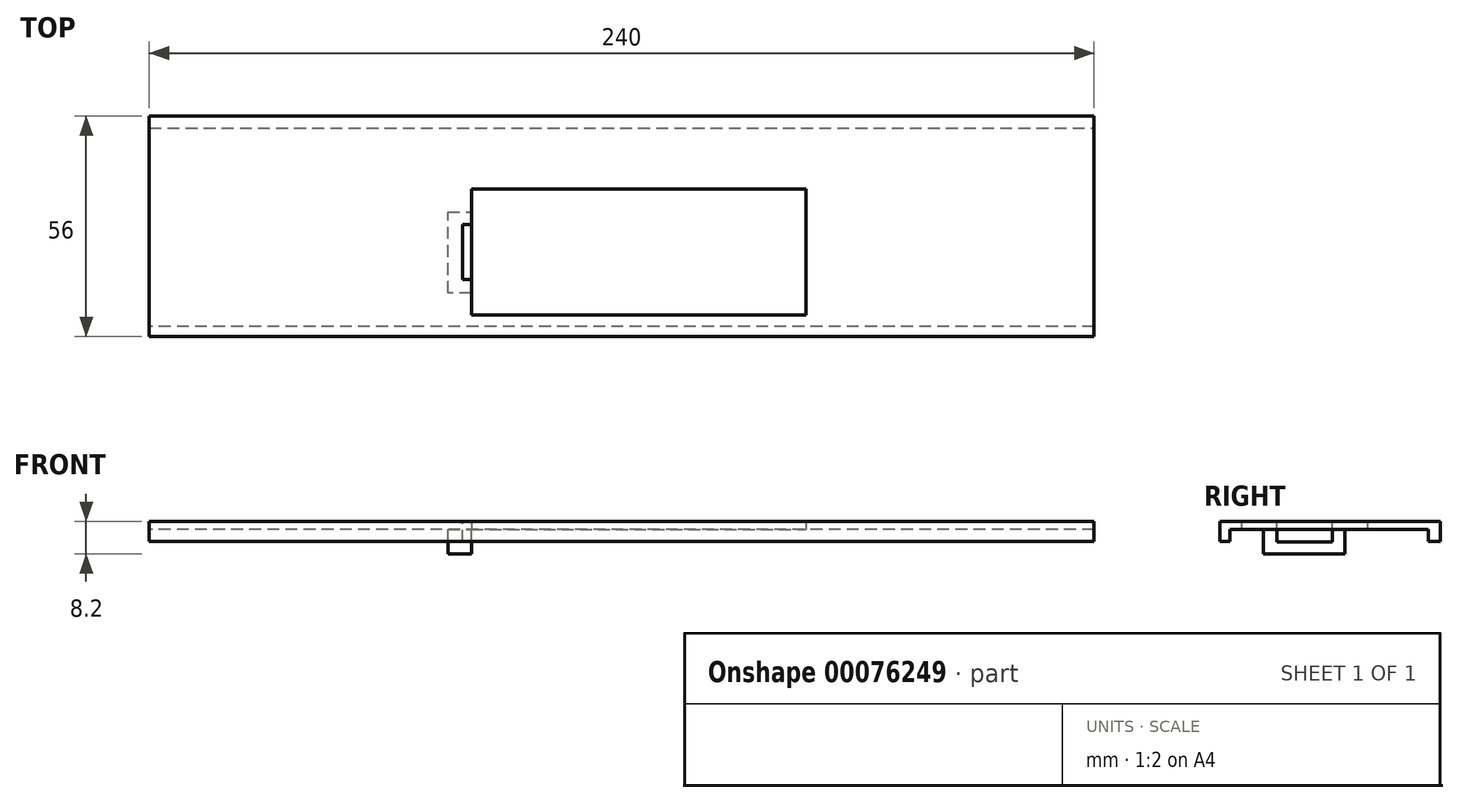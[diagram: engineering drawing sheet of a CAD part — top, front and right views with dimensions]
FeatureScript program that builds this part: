
annotation { "Feature Type Name" : "Feature", "Feature Type Description" : "" }
export const myFeature = defineFeature(function(context is Context, id is Id, definition is map)
    precondition{}
    {
        {
            var Q0;
            Q0=qCreatedBy(makeId("Top.planeOp"),FACE);
            var sketch = newSketch(context, id + "F0", { "sketchPlane" : qUnion([Q0])});
            skLineSegment(sketch, "E0.bottom", {"start": v(-106.36, 0) * mm, "end": v(133.64, 0) * mm});
            skLineSegment(sketch, "E0.top", {"start": v(-106.36, 56) * mm, "end": v(133.64, 56) * mm});
            skLineSegment(sketch, "E0.left", {"start": v(-106.36, 0) * mm, "end": v(-106.36, 56) * mm});
            skLineSegment(sketch, "E0.right", {"start": v(133.64, 0) * mm, "end": v(133.64, 56) * mm});
            skLineSegment(sketch, "E1.bottom", {"start": v(-24.53, 37.5) * mm, "end": v(60.47, 37.5) * mm});
            skLineSegment(sketch, "E1.top", {"start": v(-24.53, 5.5) * mm, "end": v(60.47, 5.5) * mm});
            skLineSegment(sketch, "E1.left", {"start": v(-24.53, 37.5) * mm, "end": v(-24.53, 5.5) * mm});
            skLineSegment(sketch, "E1.right", {"start": v(60.47, 37.5) * mm, "end": v(60.47, 5.5) * mm});
            skSolve(sketch);
        }
        {
            var Q0;
            Q0=makeQuery(id+"F0.imprint","IMPRINT",FACE,{"disambiguationData":[TD([[makeQuery(id+"F0.imprint","IMPRINT",EDGE,{"derivedFrom":sQuery(id+"F0.wireOp",EDGE,"E0.bottom")}),1.0]])]});
            extrude(context, id + "F1", {"entities" : qUnion([Q0]), "depth" : 2 * mm});
        }
        {
            var Q0;
            Q0=makeQuery(id+"F1.opExtrude","CAP_FACE",FACE,{"disambiguationData":[OSD([sQuery(id+"F0.wireOp",EDGE,"E0.bottom"),sQuery(id+"F0.wireOp",EDGE,"E0.top"),sQuery(id+"F0.wireOp",EDGE,"E0.left"),sQuery(id+"F0.wireOp",EDGE,"E0.right"),sQuery(id+"F0.wireOp",EDGE,"E1.bottom"),sQuery(id+"F0.wireOp",EDGE,"E1.top"),sQuery(id+"F0.wireOp",EDGE,"E1.left"),sQuery(id+"F0.wireOp",EDGE,"E1.right")])],"isStart":false});
            var sketch = newSketch(context, id + "F2", { "sketchPlane" : qUnion([Q0])});
            skLineSegment(sketch, "E2", {"start": v(-24.53, 37.5) * mm, "end": v(-24.53, 28.5) * mm});
            skLineSegment(sketch, "E3", {"start": v(-24.53, 5.5) * mm, "end": v(-24.53, 14.5) * mm});
            skLineSegment(sketch, "E4", {"start": v(-24.53, 14.5) * mm, "end": v(-26.73, 14.5) * mm});
            skLineSegment(sketch, "E5", {"start": v(-24.53, 28.5) * mm, "end": v(-26.73, 28.5) * mm});
            skLineSegment(sketch, "E6", {"start": v(-26.73, 14.5) * mm, "end": v(-26.73, 28.5) * mm});
            skSolve(sketch);
        }
        {
            var Q0;
            {var subQ0=sQuery(id+"F2.wireOp",EDGE,"E4");Q0=makeQuery(id+"F2.imprint","IMPRINT",FACE,{"disambiguationData":[TD([[makeQuery(id+"F2.imprint","IMPRINT",EDGE,{"derivedFrom":subQ0}),-1.0]])]});}
            extrude(context, id + "F3", {"entities" : qUnion([Q0]), "operationType" : NewBodyOperationType.REMOVE, "oppositeDirection" : true, "depth" : 25 * mm});
        }
        {
            var Q0;
            Q0=makeQuery(id+"F1.opExtrude","CAP_FACE",FACE,{"disambiguationData":[OSD([sQuery(id+"F0.wireOp",EDGE,"E0.bottom"),sQuery(id+"F0.wireOp",EDGE,"E0.top"),sQuery(id+"F0.wireOp",EDGE,"E0.left"),sQuery(id+"F0.wireOp",EDGE,"E0.right"),sQuery(id+"F0.wireOp",EDGE,"E1.bottom"),sQuery(id+"F0.wireOp",EDGE,"E1.top"),sQuery(id+"F0.wireOp",EDGE,"E1.left"),sQuery(id+"F0.wireOp",EDGE,"E1.right")])],"isStart":true});
            var sketch = newSketch(context, id + "F4", { "sketchPlane" : qUnion([Q0])});
            skLineSegment(sketch, "E7", {"start": v(-24.53, -11.05) * mm, "end": v(-30.5, -11.05) * mm});
            skLineSegment(sketch, "E8", {"start": v(-30.5, -11.05) * mm, "end": v(-30.5, -31.68) * mm});
            skLineSegment(sketch, "E9", {"start": v(-24.53, -31.68) * mm, "end": v(-24.53, -28.5) * mm});
            skLineSegment(sketch, "E10", {"start": v(-24.53, -28.5) * mm, "end": v(-26.73, -28.5) * mm});
            skLineSegment(sketch, "E11", {"start": v(-26.73, -28.5) * mm, "end": v(-26.73, -14.5) * mm});
            skLineSegment(sketch, "E12", {"start": v(-26.73, -14.5) * mm, "end": v(-24.53, -14.5) * mm});
            skLineSegment(sketch, "E13", {"start": v(-24.53, -14.5) * mm, "end": v(-24.53, -11.05) * mm});
            skLineSegment(sketch, "E14", {"start": v(-30.5, -31.68) * mm, "end": v(-24.53, -31.68) * mm});
            skSolve(sketch);
        }
        {
            var Q0;
            Q0=makeQuery(id+"F4.imprint","IMPRINT",FACE,{"disambiguationData":[TD([[makeQuery(id+"F4.imprint","IMPRINT",EDGE,{"derivedFrom":sQuery(id+"F4.wireOp",EDGE,"E7")}),1.0]])]});
            extrude(context, id + "F5", {"entities" : qUnion([Q0]), "operationType" : NewBodyOperationType.ADD, "depth" : 3.2 * mm});
        }
        {
            var Q0;
            Q0=makeQuery(id+"F5.opExtrude","CAP_FACE",FACE,{"disambiguationData":[OSD([sQuery(id+"F4.wireOp",EDGE,"E7"),sQuery(id+"F4.wireOp",EDGE,"E8"),sQuery(id+"F4.wireOp",EDGE,"E9"),sQuery(id+"F4.wireOp",EDGE,"E10"),sQuery(id+"F4.wireOp",EDGE,"E11"),sQuery(id+"F4.wireOp",EDGE,"E12"),sQuery(id+"F4.wireOp",EDGE,"E13"),sQuery(id+"F4.wireOp",EDGE,"E14")])],"isStart":false});
            var sketch = newSketch(context, id + "F6", { "sketchPlane" : qUnion([Q0])});
            skLineSegment(sketch, "E15.bottom", {"start": v(-24.53, -11.05) * mm, "end": v(-30.5, -11.05) * mm});
            skLineSegment(sketch, "E15.top", {"start": v(-24.53, -31.68) * mm, "end": v(-30.5, -31.68) * mm});
            skLineSegment(sketch, "E15.left", {"start": v(-24.53, -11.05) * mm, "end": v(-24.53, -31.68) * mm});
            skLineSegment(sketch, "E15.right", {"start": v(-30.5, -11.05) * mm, "end": v(-30.5, -31.68) * mm});
            skSolve(sketch);
        }
        {
            var Q0;
            {var subQ4=sQuery(id+"F6.wireOp",EDGE,"E15.bottom");Q0=makeQuery(id+"F6.imprint","IMPRINT",FACE,{"disambiguationData":[TD([[makeQuery(id+"F6.imprint","IMPRINT",EDGE,{"derivedFrom":subQ4}),1.0]])]});}
            var Q1;
            {var subQ1=makeQuery(id+"F5.opExtrude","CAP_EDGE",EDGE,{"disambiguationData":[OSD([sQuery(id+"F4.wireOp",EDGE,"E10")])],"isStart":false});Q1=makeQuery(id+"F6.imprint","IMPRINT",FACE,{"disambiguationData":[TD([[makeQuery(id+"F6.imprint","IMPRINT",EDGE,{"derivedFrom":subQ1}),-1.0]])]});}
            extrude(context, id + "F7", {"entities" : qUnion([Q0, Q1]), "operationType" : NewBodyOperationType.ADD, "depth" : 3 * mm});
        }
        {
            var Q0;
            Q0=makeQuery(id+"F1.opExtrude","CAP_FACE",FACE,{"disambiguationData":[OSD([sQuery(id+"F0.wireOp",EDGE,"E0.bottom"),sQuery(id+"F0.wireOp",EDGE,"E0.top"),sQuery(id+"F0.wireOp",EDGE,"E0.left"),sQuery(id+"F0.wireOp",EDGE,"E0.right"),sQuery(id+"F0.wireOp",EDGE,"E1.bottom"),sQuery(id+"F0.wireOp",EDGE,"E1.top"),sQuery(id+"F0.wireOp",EDGE,"E1.left"),sQuery(id+"F0.wireOp",EDGE,"E1.right")])],"isStart":true});
            var sketch = newSketch(context, id + "F8", { "sketchPlane" : qUnion([Q0])});
            skLineSegment(sketch, "E16.bottom", {"start": v(133.64, 0) * mm, "end": v(-106.36, 0) * mm});
            skLineSegment(sketch, "E16.top", {"start": v(133.64, -2.5) * mm, "end": v(-106.36, -2.5) * mm});
            skLineSegment(sketch, "E16.left", {"start": v(133.64, 0) * mm, "end": v(133.64, -2.5) * mm});
            skLineSegment(sketch, "E16.right", {"start": v(-106.36, 0) * mm, "end": v(-106.36, -2.5) * mm});
            skLineSegment(sketch, "E17.bottom", {"start": v(-106.36, -56) * mm, "end": v(133.64, -56) * mm});
            skLineSegment(sketch, "E17.top", {"start": v(-106.36, -53) * mm, "end": v(133.64, -53) * mm});
            skLineSegment(sketch, "E17.left", {"start": v(-106.36, -56) * mm, "end": v(-106.36, -53) * mm});
            skLineSegment(sketch, "E17.right", {"start": v(133.64, -56) * mm, "end": v(133.64, -53) * mm});
            skSolve(sketch);
        }
        {
            var Q0;
            Q0=makeQuery(id+"F8.imprint","IMPRINT",FACE,{"disambiguationData":[TD([[makeQuery(id+"F8.imprint","IMPRINT",EDGE,{"derivedFrom":sQuery(id+"F8.wireOp",EDGE,"E17.bottom")}),1.0]])]});
            extrude(context, id + "F9", {"entities" : qUnion([Q0]), "operationType" : NewBodyOperationType.ADD, "depth" : 3 * mm});
        }
        {
            var Q0;
            Q0=makeQuery(id+"F8.imprint","IMPRINT",FACE,{"disambiguationData":[TD([[makeQuery(id+"F8.imprint","IMPRINT",EDGE,{"derivedFrom":sQuery(id+"F8.wireOp",EDGE,"E16.bottom")}),-1.0]])]});
            extrude(context, id + "F10", {"entities" : qUnion([Q0]), "operationType" : NewBodyOperationType.ADD, "depth" : 3 * mm});
        }
    });
